# Revit family: Woodfold-Accordion-Door-Family-Series-240
name_source: partatom
category: Doors
units: mm (PartAtom-declared; Revit-internal decimal feet)

## family parameters
Always vertical = Yes
Cut with Voids When Loaded = No
Host = Wall
Room Calculation Point = No
Shared = No

## types (5) — shared parameters
Description = Accordion door
Frame Material = Default
Frame Projection Ext. = 0' - 1"
Frame Projection Int. = 0' - 1"
Frame Width = 0' - 3"
Function = Interior
Manufacturer = Woodfold Mfg., Inc.
Model = 240
Panel Connectors = Flexible Vinyl
Type Comments = Width: No limitation.  Height: Vinyl-Lam up to 12'-1", Hardwoods up to 10'-1"
URL = www.woodfold.com
Wall Closure = By host

## per-type parameters (varying)
| type | Frame Visibility | Hardware Type | Height | Lead Post | Panel Material | Recessed Track | Sliding Jamb | Stack Dimension | Surface Jamb | Surface Track | Track Material | Width |
| 8'-0" x 8'-0" Recessed Track | Yes | Keylock two sides | 8' - 0" | Metal - Aluminum | Woodfold - Cherry | Yes | No | 0' - 10 1/4" | Yes | No | Metal - Aluminum | 6' - 0" |
| 8'-0" x 8'-0" Surface Mounted w/Deadlatch | Yes | Deadlatch with Thumbturn Two-side | 8' - 0" | Metal - Aluminum | Woodfold - Cherry | No | No | 0' - 10 1/4" | Yes | Yes | Metal - Aluminum | 6' - 0" |
| 8'-0" x 8'-0" Surface Mounted w/Magnetic Catch | Yes | Magnetic Catch & Strick Plate | 8' - 0" | Metal - Aluminum | Woodfold - Cherry | No | No | 0' - 10 1/4" | Yes | Yes | Metal - Aluminum | 6' - 0" |
| 6'-0" x 8'-0" Surface Track | Yes | Deadlatch with Thumbturn Two-side | 8' - 0" | Metal - Aluminum | Woodfold - Dark Oak | No | No | 0' - 10 1/4" | Yes | Yes | Metal - Aluminum | 6' - 0" |
| 12'-0" x 9'-0" RecessedTrack, Sliding Jamb | No | Deadlatch with Thumbturn Two-side | 9' - 0" | Woodfold - Aluminum - Bronze | Woodfold - Birch | Yes | Yes | 1' - 5 3/4" | No | No | Woodfold - Aluminum - Bronze | 12' - 0" |

## geometry (parser evidence)
native form markers: Sweep x22
no freeform markers — native parametric forms only
